# Revit family: Counterweight
name_source: partatom
category: Generic Models
units: mm (PartAtom-declared; Revit-internal decimal feet)

## family parameters
Always vertical = Yes
Can host rebar = No
Cut with Voids When Loaded = No
Maintain Annotation Orientation = No
Part Type = Normal
Room Calculation Point = No
Round Connector Dimension = Use Diameter
Shared = No
Work Plane-Based = No

## types (1)
- Counterweight
    Bottom Part Height = 241 mm
    CounterWeight_Weight = 1500
    Default Elevation = 0 mm  [stored 0 ft]
    Frame Height = 2500 mm  [stored 8.2021 ft]
    Frame Inner Length = 50 mm
    Frame Insert = 120 mm  [stored 0.393701 ft]
    Frame Length = 250 mm  [stored 0.82021 ft]
    Frame Thickness = 23 mm
    Frame Width = 1400 mm  [stored 4.59318 ft]
    LiftSheave_Diameter = 400
    Strike Plate Height = 538 mm
    Strike Plate Length = 227 mm
    Strike Plate Width = 200 mm  [stored 0.656168 ft]
    Top Part Height = 250 mm  [stored 0.82021 ft]
    Weight Plate Length = 204 mm
    Weight Plate Offset = 60 mm  [stored 0.19685 ft]
    Weight Plate Thickness = 60 mm  [stored 0.19685 ft]
    Weight Plate Width = 2634 mm

note: [stored X ft] marks values corroborated as IEEE doubles in the binary element streams (Revit-internal decimal feet)

## geometry (parser evidence)
native form markers: Sweep x2
no freeform markers — native parametric forms only
